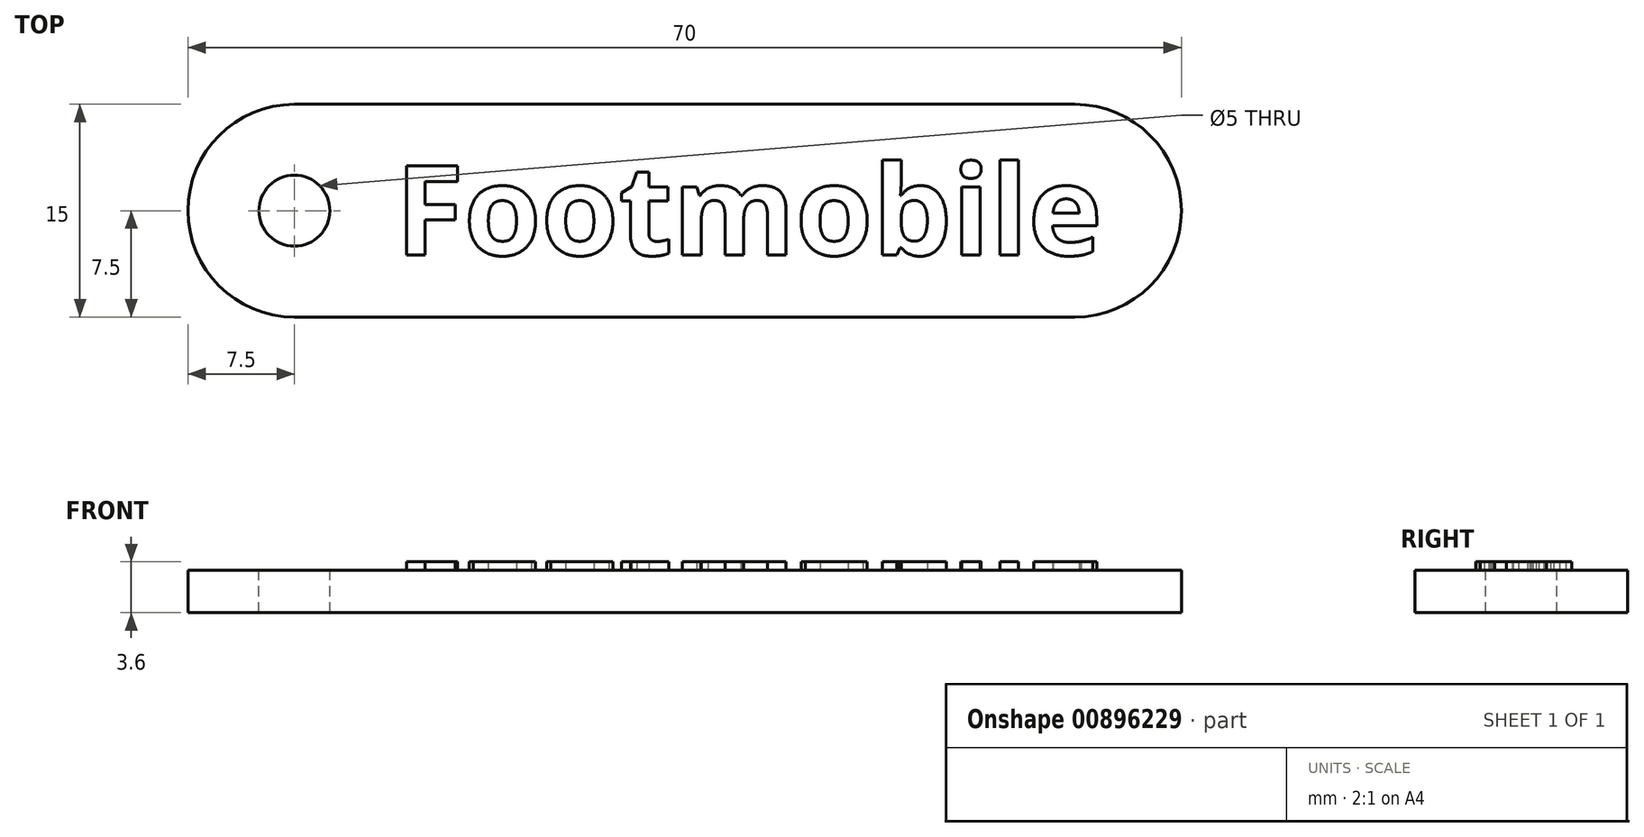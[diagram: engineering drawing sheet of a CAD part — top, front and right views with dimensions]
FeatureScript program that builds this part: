
annotation { "Feature Type Name" : "Feature", "Feature Type Description" : "" }
export const myFeature = defineFeature(function(context is Context, id is Id, definition is map)
    precondition{}
    {
        {
            var Q0;
            Q0=qCreatedBy(makeId("Top.planeOp"),FACE);
            var sketch = newSketch(context, id + "F0", { "sketchPlane" : qUnion([Q0])});
            skLineSegment(sketch, "E0.bottom", {"start": v(0, 0) * mm, "end": v(70, 0) * mm});
            skLineSegment(sketch, "E0.top", {"start": v(0, -15) * mm, "end": v(70, -15) * mm});
            skLineSegment(sketch, "E0.left", {"start": v(0, 0) * mm, "end": v(0, -15) * mm});
            skLineSegment(sketch, "E0.right", {"start": v(70, 0) * mm, "end": v(70, -15) * mm});
            skLineSegment(sketch, "E1", {"start": v(0, -7.5) * mm, "end": v(7.5, -7.5) * mm, "construction": true});
            skCircle(sketch, "E2", {"center": v(7.5, -7.5) * mm, "radius": 2.5 * mm});
            skSolve(sketch);
        }
        {
            var Q0;
            Q0=qCreatedBy(makeId("Top.planeOp"),FACE);
            var sketch = newSketch(context, id + "F1", { "sketchPlane" : qUnion([Q0])});
            skText(sketch, "E3", { "text": "Footmobile", "fontName": "OpenSans-Bold.ttf"});
            const initialGuessF1  = {"E3": [0.0146, -0.01063, 1, 0, 0.00634]};
            skSetInitialGuess(sketch, initialGuessF1);
            skSolve(sketch);
        }
        {
            var Q0;
            Q0=makeQuery(id+"F0.imprint","IMPRINT",FACE,{"disambiguationData":[TD([[makeQuery(id+"F0.imprint","IMPRINT",EDGE,{"derivedFrom":sQuery(id+"F0.wireOp",EDGE,"E0.bottom")}),-1.0]])]});
            extrude(context, id + "F2", {"entities" : qUnion([Q0]), "oppositeDirection" : true, "depth" : 3 * mm, "offsetDistance" : 25 * mm});
        }
        {
            var Q0;
            Q0 = qSketchRegion(id + "F1", true);
            extrude(context, id + "F3", {"entities" : qUnion([Q0]), "operationType" : NewBodyOperationType.ADD, "depth" : 0.6 * mm, "offsetDistance" : 25 * mm});
        }
        {
            var Q0;
            Q0=makeQuery(id+"F2.opExtrude","SWEPT_EDGE",EDGE,{"disambiguationData":[OSD([sQuery(id+"F0.wireOp",EDGE,"E0.top"),sQuery(id+"F0.wireOp",EDGE,"E0.left")])]});
            var Q1;
            Q1=makeQuery(id+"F2.opExtrude","SWEPT_EDGE",EDGE,{"disambiguationData":[OSD([sQuery(id+"F0.wireOp",EDGE,"E0.top"),sQuery(id+"F0.wireOp",EDGE,"E0.right")])]});
            var Q2;
            Q2=makeQuery(id+"F2.opExtrude","SWEPT_EDGE",EDGE,{"disambiguationData":[OSD([sQuery(id+"F0.wireOp",EDGE,"E0.bottom"),sQuery(id+"F0.wireOp",EDGE,"E0.right")])]});
            var Q3;
            Q3=makeQuery(id+"F2.opExtrude","SWEPT_EDGE",EDGE,{"disambiguationData":[OSD([sQuery(id+"F0.wireOp",EDGE,"E0.bottom"),sQuery(id+"F0.wireOp",EDGE,"E0.left")])]});
            fillet(context, id + "F4", {"entities" : qUnion([Q0, Q1, Q2, Q3]), "radius" : 7.5 * mm, "tangentPropagation" : true, "allowEdgeOverflow" : false});
        }
    });
